# Revit family: Lighting-Stradale-GEWISS-STREET[O3]-STAFFA_PALO_DOPPIA
name_source: partatom
category: Apparecchi per illuminazione
units: mm (PartAtom-declared; Revit-internal decimal feet)

## family parameters
Basato su piano di lavoro = Sì
Condiviso = No
Numero OmniClass = 23.80.00.00
Punto di calcolo locali = No
Quota connettore circolare = Usa diametro
Sempre verticale = No
Sorgente d'illuminazione = No
Taglio con vuoti quando caricato = No
Tipo di parte = Normale
Titolo OmniClass = Electric Power and Lighting

## types (1)
- GW87582 - Acciaio zincato - Grigio grafite - Doppia
    Altezza da terra testa staffa = 822 mm
    Catalogo = LIGHTING
    Catalogo Serie = STREET [O3]
    Codice EAN = 8011564783041
    Codice Electrocod = 240
    Colore = Grigio grafite
    Descrizione = STREET STAFFA TESTA PALO DOPPIA GRIGIO GRAFITE
    Descrizione: = Staffa testa palo doppia
    Dimensioni = Ã˜ 60 mm
    Dimensioni (mm) = Ã˜ 60 mm
    IDF = 38bce6fd-7d71-470c-a61e-19d51e9b6874
    IDT = df385655-572c-45cd-afe2-85265a4e7826
    Immagine tipo = GW87582.jpg
    L_staffa = 120 mm  [stored 0.393701 ft]
    Lunghezza = 1+1 m
    Materiale = Acciaio zincato
    Modello = GW87582
    Peso (kg) = 11,5
    Peso (kg): = 11,5
    Produttore = GEWISS S.p.A.
    Prospetto di default = 1219 mm
    SEO = Staffa
    Scheda Tecnica = https://www.gewiss.com
    Supporti = <Per categoria>
    Tubolare = <Per categoria>
    URL = https://www.gewiss.com
    Versione file RFA = 20.11

note: [stored X ft] marks values corroborated as IEEE doubles in the binary element streams (Revit-internal decimal feet)

## geometry (parser evidence)
native form markers: Blend x4
no freeform markers — native parametric forms only
